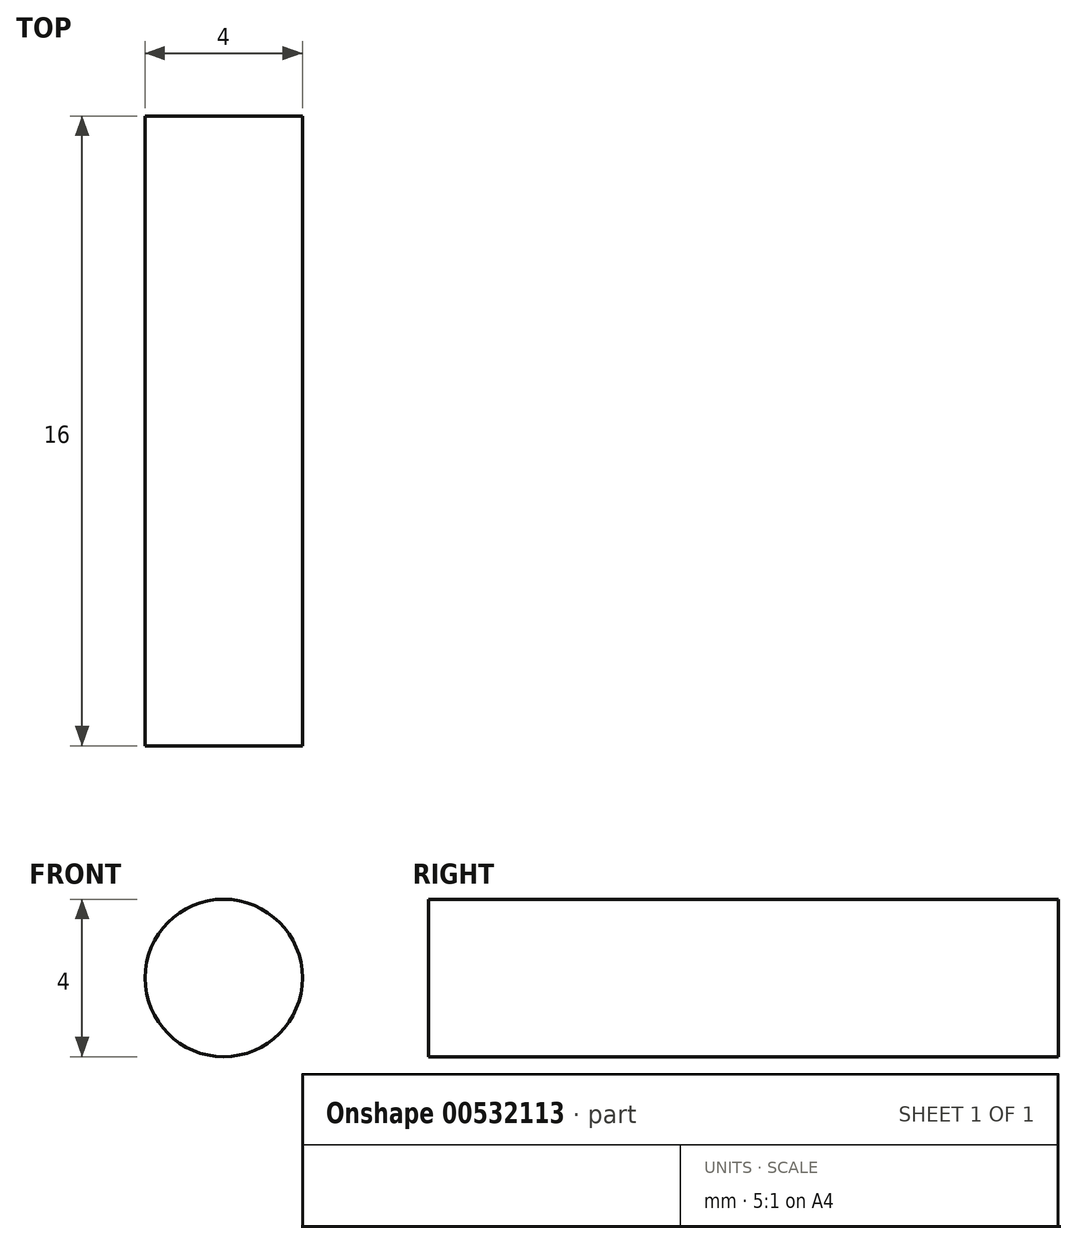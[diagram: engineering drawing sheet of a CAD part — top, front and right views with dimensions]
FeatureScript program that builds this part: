
annotation { "Feature Type Name" : "Feature", "Feature Type Description" : "" }
export const myFeature = defineFeature(function(context is Context, id is Id, definition is map)
    precondition{}
    {
        {
            var Q0;
            Q0=qCreatedBy(makeId("Front.planeOp"),FACE);
            var sketch = newSketch(context, id + "F0", { "sketchPlane" : qUnion([Q0])});
            skCircle(sketch, "E0", {"center": v(0, 0) * mm, "radius": 2 * mm});
            skSolve(sketch);
        }
        {
            var Q0;
            Q0=qSketchRegion(id+"F0",true);
            extrude(context, id + "F1", {"entities" : qUnion([Q0]), "depth" : 16 * mm, "offsetDistance" : 25.4 * mm});
        }
    });
